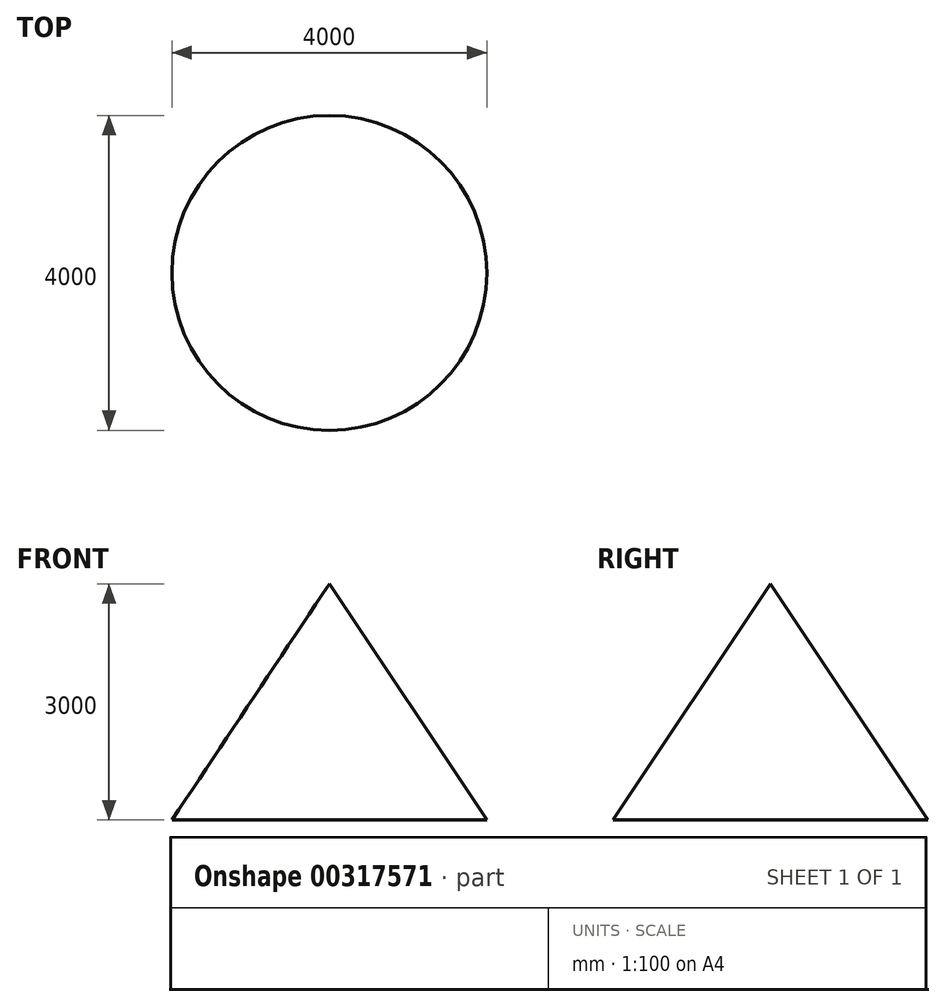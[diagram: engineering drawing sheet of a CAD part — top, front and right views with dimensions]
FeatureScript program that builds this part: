
annotation { "Feature Type Name" : "Feature", "Feature Type Description" : "" }
export const myFeature = defineFeature(function(context is Context, id is Id, definition is map)
    precondition{}
    {
        {
            var Q0;
            Q0=qCreatedBy(makeId("Front.planeOp"),FACE);
            var sketch = newSketch(context, id + "F0", { "sketchPlane" : qUnion([Q0])});
            skLineSegment(sketch, "E0", {"start": v(0, 0) * mm, "end": v(2000, 0) * mm});
            skLineSegment(sketch, "E1", {"start": v(2000, 0) * mm, "end": v(0, 3000) * mm});
            skLineSegment(sketch, "E2", {"start": v(0, 3000) * mm, "end": v(0, 0) * mm});
            skSolve(sketch);
        }
        {
            var Q0;
            Q0=makeQuery(id+"F0.imprint","IMPRINT",FACE,{"disambiguationData":[TD([[makeQuery(id+"F0.imprint","IMPRINT",EDGE,{"derivedFrom":sQuery(id+"F0.wireOp",EDGE,"E0")}),1.0]])]});
            var Q1;
            Q1=sQuery(id+"F0.wireOp",EDGE,"E2");
            revolve(context, id + "F1", {"entities" : qUnion([Q0]), "axis" : qUnion([Q1]), "revolveType" : RevolveType.FULL});
        }
    });
